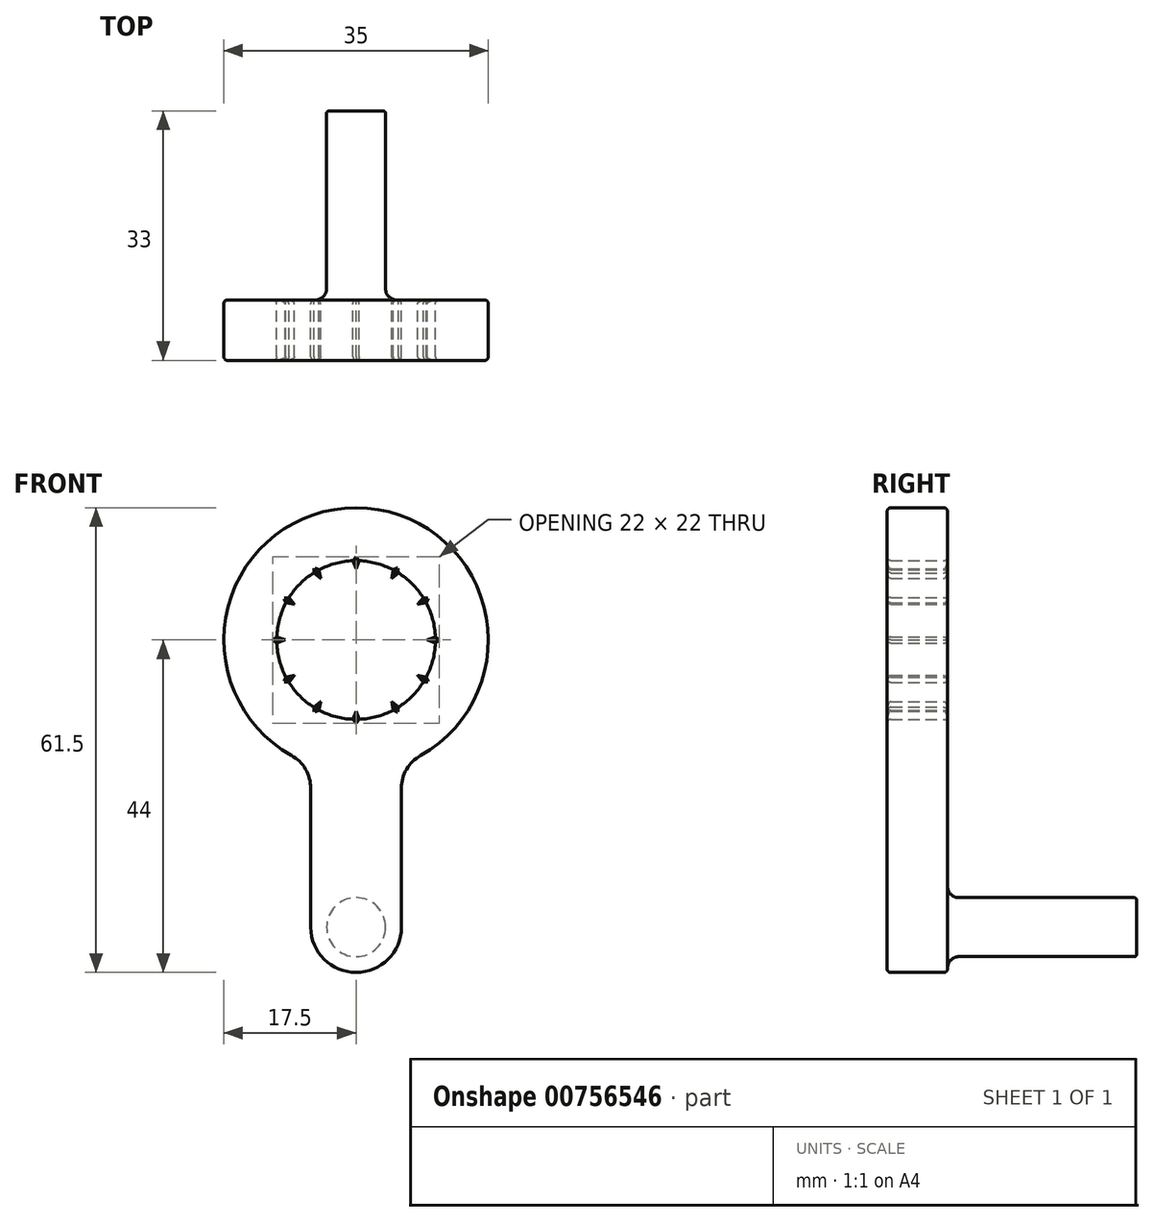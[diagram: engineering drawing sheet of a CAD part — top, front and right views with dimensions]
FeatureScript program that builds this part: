
annotation { "Feature Type Name" : "Feature", "Feature Type Description" : "" }
export const myFeature = defineFeature(function(context is Context, id is Id, definition is map)
    precondition{}
    {
        {
            var Q0;
            Q0=qCreatedBy(makeId("Front.planeOp"),FACE);
            var sketch = newSketch(context, id + "F0", { "sketchPlane" : qUnion([Q0])});
            skArc(sketch, "E0", {"start": v(8.56, -15.27) * mm, "mid": v(0, 17.5) * mm, "end": v(-8.56, -15.27) * mm});
            skCircle(sketch, "E1", {"center": v(0, 0) * mm, "radius": 9.4 * mm, "construction": true});
            skLineSegment(sketch, "E2", {"start": v(0, 109.46) * mm, "end": v(0, -98.11) * mm, "construction": true});
            skLineSegment(sketch, "E3", {"start": v(-338.44, 0) * mm, "end": v(369.24, 0) * mm, "construction": true});
            skLineSegment(sketch, "E4", {"start": v(-0.4, 10.5) * mm, "end": v(0, 9.4) * mm});
            skLineSegment(sketch, "E5.MirrorCS", {"start": v(0.4, 10.5) * mm, "end": v(0, 9.4) * mm});
            skLineSegment(sketch, "E6", {"start": v(0, 0) * mm, "end": v(63.84, 110.57) * mm, "construction": true});
            skArc(sketch, "E7", {"start": v(4.9, 9.29) * mm, "mid": v(2.72, 10.14) * mm, "end": v(0.4, 10.5) * mm});
            skLineSegment(sketch, "E8", {"start": v(0, 0) * mm, "end": v(0, -28.63) * mm, "construction": true});
            skLineSegment(sketch, "E9", {"start": v(-6, -19.63) * mm, "end": v(-6, -38) * mm});
            skLineSegment(sketch, "E10", {"start": v(0, -44) * mm, "end": v(0, -44) * mm});
            skLineSegment(sketch, "E11", {"start": v(6, -38) * mm, "end": v(6, -19.63) * mm});
            skPoint(sketch, "E12.visualSharp", {"position": v(-6, -44) * mm});
            skArc(sketch, "E12.filletArc", {"start": v(-6, -38) * mm, "mid": v(-4.24, -42.24) * mm, "end": v(0, -44) * mm});
            skPoint(sketch, "E13.visualSharp", {"position": v(6, -44) * mm});
            skArc(sketch, "E13.filletArc", {"start": v(0, -44) * mm, "mid": v(4.24, -42.24) * mm, "end": v(6, -38) * mm});
            skPoint(sketch, "E14.visualSharp", {"position": v(-6, -16.44) * mm});
            skArc(sketch, "E14.filletArc", {"start": v(-6, -19.63) * mm, "mid": v(-6.69, -17.1) * mm, "end": v(-8.56, -15.27) * mm});
            skPoint(sketch, "E15.visualSharp", {"position": v(6, -16.44) * mm});
            skArc(sketch, "E15.filletArc", {"start": v(8.56, -15.27) * mm, "mid": v(6.69, -17.1) * mm, "end": v(6, -19.63) * mm});
            skArc(sketch, "E16", {"start": v(1, -27.5) * mm, "mid": v(0, -26.5) * mm, "end": v(-1, -27.5) * mm, "construction": true});
            skArc(sketch, "E17", {"start": v(-1, -28) * mm, "mid": v(0, -29) * mm, "end": v(1, -28) * mm, "construction": true});
            skLineSegment(sketch, "E18", {"start": v(-1, -27.5) * mm, "end": v(-1, -28) * mm, "construction": true});
            skLineSegment(sketch, "E19", {"start": v(1, -27.5) * mm, "end": v(1, -28) * mm, "construction": true});
            skLineSegment(sketch, "E20.1.0", {"start": v(-4.9, 9.29) * mm, "end": v(-4.7, 8.14) * mm});
            skLineSegment(sketch, "E20.1.1", {"start": v(-5.6, 8.89) * mm, "end": v(-4.7, 8.14) * mm});
            skArc(sketch, "E20.1.2", {"start": v(-0.4, 10.5) * mm, "mid": v(-2.72, 10.14) * mm, "end": v(-4.9, 9.29) * mm});
            skLineSegment(sketch, "E20.2.0", {"start": v(-8.89, 5.6) * mm, "end": v(-8.14, 4.7) * mm});
            skLineSegment(sketch, "E20.2.1", {"start": v(-9.29, 4.9) * mm, "end": v(-8.14, 4.7) * mm});
            skArc(sketch, "E20.2.2", {"start": v(-5.6, 8.89) * mm, "mid": v(-7.42, 7.42) * mm, "end": v(-8.89, 5.6) * mm});
            skLineSegment(sketch, "E21.2.3.0", {"start": v(-10.5, 0.4) * mm, "end": v(-9.4, 0) * mm});
            skLineSegment(sketch, "E21.3.3.0", {"start": v(-10.5, -0.4) * mm, "end": v(-9.4, 0) * mm});
            skArc(sketch, "E21.6.3.0", {"start": v(-9.29, 4.9) * mm, "mid": v(-10.14, 2.72) * mm, "end": v(-10.5, 0.4) * mm});
            skLineSegment(sketch, "E21.2.4.0", {"start": v(-9.29, -4.9) * mm, "end": v(-8.14, -4.7) * mm});
            skLineSegment(sketch, "E21.3.4.0", {"start": v(-8.89, -5.6) * mm, "end": v(-8.14, -4.7) * mm});
            skArc(sketch, "E21.6.4.0", {"start": v(-10.5, -0.4) * mm, "mid": v(-10.14, -2.72) * mm, "end": v(-9.29, -4.9) * mm});
            skLineSegment(sketch, "E21.2.5.0", {"start": v(-5.6, -8.89) * mm, "end": v(-4.7, -8.14) * mm});
            skLineSegment(sketch, "E21.3.5.0", {"start": v(-4.9, -9.29) * mm, "end": v(-4.7, -8.14) * mm});
            skArc(sketch, "E21.6.5.0", {"start": v(-8.89, -5.6) * mm, "mid": v(-7.42, -7.42) * mm, "end": v(-5.6, -8.89) * mm});
            skLineSegment(sketch, "E21.2.6.0", {"start": v(-0.4, -10.5) * mm, "end": v(0, -9.4) * mm});
            skLineSegment(sketch, "E21.3.6.0", {"start": v(0.4, -10.5) * mm, "end": v(0, -9.4) * mm});
            skArc(sketch, "E21.6.6.0", {"start": v(-4.9, -9.29) * mm, "mid": v(-2.72, -10.14) * mm, "end": v(-0.4, -10.5) * mm});
            skLineSegment(sketch, "E21.2.7.0", {"start": v(4.9, -9.29) * mm, "end": v(4.7, -8.14) * mm});
            skLineSegment(sketch, "E21.3.7.0", {"start": v(5.6, -8.89) * mm, "end": v(4.7, -8.14) * mm});
            skArc(sketch, "E21.6.7.0", {"start": v(0.4, -10.5) * mm, "mid": v(2.72, -10.14) * mm, "end": v(4.9, -9.29) * mm});
            skLineSegment(sketch, "E21.2.8.0", {"start": v(8.89, -5.6) * mm, "end": v(8.14, -4.7) * mm});
            skLineSegment(sketch, "E21.3.8.0", {"start": v(9.29, -4.9) * mm, "end": v(8.14, -4.7) * mm});
            skArc(sketch, "E21.6.8.0", {"start": v(5.6, -8.89) * mm, "mid": v(7.42, -7.42) * mm, "end": v(8.89, -5.6) * mm});
            skLineSegment(sketch, "E21.2.9.0", {"start": v(10.5, -0.4) * mm, "end": v(9.4, 0) * mm});
            skLineSegment(sketch, "E21.3.9.0", {"start": v(10.5, 0.4) * mm, "end": v(9.4, 0) * mm});
            skArc(sketch, "E21.6.9.0", {"start": v(9.29, -4.9) * mm, "mid": v(10.14, -2.72) * mm, "end": v(10.5, -0.4) * mm});
            skLineSegment(sketch, "E21.2.10.0", {"start": v(9.29, 4.9) * mm, "end": v(8.14, 4.7) * mm});
            skLineSegment(sketch, "E21.3.10.0", {"start": v(8.89, 5.6) * mm, "end": v(8.14, 4.7) * mm});
            skArc(sketch, "E21.6.10.0", {"start": v(10.5, 0.4) * mm, "mid": v(10.14, 2.72) * mm, "end": v(9.29, 4.9) * mm});
            skLineSegment(sketch, "E21.2.11.0", {"start": v(5.6, 8.89) * mm, "end": v(4.7, 8.14) * mm});
            skLineSegment(sketch, "E21.3.11.0", {"start": v(4.9, 9.29) * mm, "end": v(4.7, 8.14) * mm});
            skArc(sketch, "E21.6.11.0", {"start": v(8.89, 5.6) * mm, "mid": v(7.42, 7.42) * mm, "end": v(5.6, 8.89) * mm});
            skSolve(sketch);
        }
        {
            var Q0;
            Q0=makeQuery(id+"F0.imprint","IMPRINT",FACE,{"disambiguationData":[TD([[makeQuery(id+"F0.imprint","IMPRINT",EDGE,{"derivedFrom":sQuery(id+"F0.wireOp",EDGE,"E0")}),1.0]])]});
            extrude(context, id + "F1", {"entities" : qUnion([Q0]), "depth" : 8 * mm, "offsetDistance" : 25 * mm});
        }
        {
            var Q0;
            Q0=makeQuery(id+"F1.opExtrude","CAP_FACE",FACE,{"disambiguationData":[OSD([sQuery(id+"F0.wireOp",EDGE,"E0"),sQuery(id+"F0.wireOp",EDGE,"E4"),sQuery(id+"F0.wireOp",EDGE,"E5.MirrorCS"),sQuery(id+"F0.wireOp",EDGE,"E7"),sQuery(id+"F0.wireOp",EDGE,"E9"),sQuery(id+"F0.wireOp",EDGE,"E10"),sQuery(id+"F0.wireOp",EDGE,"E11"),sQuery(id+"F0.wireOp",EDGE,"E12.filletArc"),sQuery(id+"F0.wireOp",EDGE,"E13.filletArc"),sQuery(id+"F0.wireOp",EDGE,"E14.filletArc"),sQuery(id+"F0.wireOp",EDGE,"E15.filletArc"),sQuery(id+"F0.wireOp",EDGE,"E20.1.0"),sQuery(id+"F0.wireOp",EDGE,"E20.1.1"),sQuery(id+"F0.wireOp",EDGE,"E20.1.2"),sQuery(id+"F0.wireOp",EDGE,"E20.2.0"),sQuery(id+"F0.wireOp",EDGE,"E20.2.1"),sQuery(id+"F0.wireOp",EDGE,"E20.2.2"),sQuery(id+"F0.wireOp",EDGE,"E21.2.3.0"),sQuery(id+"F0.wireOp",EDGE,"E21.3.3.0"),sQuery(id+"F0.wireOp",EDGE,"E21.6.3.0"),sQuery(id+"F0.wireOp",EDGE,"E21.2.4.0"),sQuery(id+"F0.wireOp",EDGE,"E21.3.4.0"),sQuery(id+"F0.wireOp",EDGE,"E21.6.4.0"),sQuery(id+"F0.wireOp",EDGE,"E21.2.5.0"),sQuery(id+"F0.wireOp",EDGE,"E21.3.5.0"),sQuery(id+"F0.wireOp",EDGE,"E21.6.5.0"),sQuery(id+"F0.wireOp",EDGE,"E21.2.6.0"),sQuery(id+"F0.wireOp",EDGE,"E21.3.6.0"),sQuery(id+"F0.wireOp",EDGE,"E21.6.6.0"),sQuery(id+"F0.wireOp",EDGE,"E21.2.7.0"),sQuery(id+"F0.wireOp",EDGE,"E21.3.7.0"),sQuery(id+"F0.wireOp",EDGE,"E21.6.7.0"),sQuery(id+"F0.wireOp",EDGE,"E21.2.8.0"),sQuery(id+"F0.wireOp",EDGE,"E21.3.8.0"),sQuery(id+"F0.wireOp",EDGE,"E21.6.8.0"),sQuery(id+"F0.wireOp",EDGE,"E21.2.9.0"),sQuery(id+"F0.wireOp",EDGE,"E21.3.9.0"),sQuery(id+"F0.wireOp",EDGE,"E21.6.9.0"),sQuery(id+"F0.wireOp",EDGE,"E21.2.10.0"),sQuery(id+"F0.wireOp",EDGE,"E21.3.10.0"),sQuery(id+"F0.wireOp",EDGE,"E21.6.10.0"),sQuery(id+"F0.wireOp",EDGE,"E21.2.11.0"),sQuery(id+"F0.wireOp",EDGE,"E21.3.11.0"),sQuery(id+"F0.wireOp",EDGE,"E21.6.11.0")])],"isStart":true});
            var sketch = newSketch(context, id + "F2", { "sketchPlane" : qUnion([Q0])});
            skSolve(sketch);
        }
        {
            var Q0;
            Q0=makeQuery(id+"F1.opExtrude","CAP_FACE",FACE,{"disambiguationData":[OSD([sQuery(id+"F0.wireOp",EDGE,"E0"),sQuery(id+"F0.wireOp",EDGE,"E4"),sQuery(id+"F0.wireOp",EDGE,"E5.MirrorCS"),sQuery(id+"F0.wireOp",EDGE,"E7"),sQuery(id+"F0.wireOp",EDGE,"E9"),sQuery(id+"F0.wireOp",EDGE,"E10"),sQuery(id+"F0.wireOp",EDGE,"E11"),sQuery(id+"F0.wireOp",EDGE,"E12.filletArc"),sQuery(id+"F0.wireOp",EDGE,"E13.filletArc"),sQuery(id+"F0.wireOp",EDGE,"E14.filletArc"),sQuery(id+"F0.wireOp",EDGE,"E15.filletArc"),sQuery(id+"F0.wireOp",EDGE,"E20.1.0"),sQuery(id+"F0.wireOp",EDGE,"E20.1.1"),sQuery(id+"F0.wireOp",EDGE,"E20.1.2"),sQuery(id+"F0.wireOp",EDGE,"E20.2.0"),sQuery(id+"F0.wireOp",EDGE,"E20.2.1"),sQuery(id+"F0.wireOp",EDGE,"E20.2.2"),sQuery(id+"F0.wireOp",EDGE,"E21.2.3.0"),sQuery(id+"F0.wireOp",EDGE,"E21.3.3.0"),sQuery(id+"F0.wireOp",EDGE,"E21.6.3.0"),sQuery(id+"F0.wireOp",EDGE,"E21.2.4.0"),sQuery(id+"F0.wireOp",EDGE,"E21.3.4.0"),sQuery(id+"F0.wireOp",EDGE,"E21.6.4.0"),sQuery(id+"F0.wireOp",EDGE,"E21.2.5.0"),sQuery(id+"F0.wireOp",EDGE,"E21.3.5.0"),sQuery(id+"F0.wireOp",EDGE,"E21.6.5.0"),sQuery(id+"F0.wireOp",EDGE,"E21.2.6.0"),sQuery(id+"F0.wireOp",EDGE,"E21.3.6.0"),sQuery(id+"F0.wireOp",EDGE,"E21.6.6.0"),sQuery(id+"F0.wireOp",EDGE,"E21.2.7.0"),sQuery(id+"F0.wireOp",EDGE,"E21.3.7.0"),sQuery(id+"F0.wireOp",EDGE,"E21.6.7.0"),sQuery(id+"F0.wireOp",EDGE,"E21.2.8.0"),sQuery(id+"F0.wireOp",EDGE,"E21.3.8.0"),sQuery(id+"F0.wireOp",EDGE,"E21.6.8.0"),sQuery(id+"F0.wireOp",EDGE,"E21.2.9.0"),sQuery(id+"F0.wireOp",EDGE,"E21.3.9.0"),sQuery(id+"F0.wireOp",EDGE,"E21.6.9.0"),sQuery(id+"F0.wireOp",EDGE,"E21.2.10.0"),sQuery(id+"F0.wireOp",EDGE,"E21.3.10.0"),sQuery(id+"F0.wireOp",EDGE,"E21.6.10.0"),sQuery(id+"F0.wireOp",EDGE,"E21.2.11.0"),sQuery(id+"F0.wireOp",EDGE,"E21.3.11.0"),sQuery(id+"F0.wireOp",EDGE,"E21.6.11.0")])],"isStart":false});
            fillet(context, id + "F3", {"entities" : qUnion([Q0]), "radius" : 0.5 * mm, "tangentPropagation" : true, "allowEdgeOverflow" : false});
        }
        {
            var Q0;
            Q0=makeQuery(id+"F1.opExtrude","CAP_FACE",FACE,{"disambiguationData":[OSD([sQuery(id+"F0.wireOp",EDGE,"E0"),sQuery(id+"F0.wireOp",EDGE,"E4"),sQuery(id+"F0.wireOp",EDGE,"E5.MirrorCS"),sQuery(id+"F0.wireOp",EDGE,"E7"),sQuery(id+"F0.wireOp",EDGE,"E9"),sQuery(id+"F0.wireOp",EDGE,"E10"),sQuery(id+"F0.wireOp",EDGE,"E11"),sQuery(id+"F0.wireOp",EDGE,"E12.filletArc"),sQuery(id+"F0.wireOp",EDGE,"E13.filletArc"),sQuery(id+"F0.wireOp",EDGE,"E14.filletArc"),sQuery(id+"F0.wireOp",EDGE,"E15.filletArc"),sQuery(id+"F0.wireOp",EDGE,"E20.1.0"),sQuery(id+"F0.wireOp",EDGE,"E20.1.1"),sQuery(id+"F0.wireOp",EDGE,"E20.1.2"),sQuery(id+"F0.wireOp",EDGE,"E20.2.0"),sQuery(id+"F0.wireOp",EDGE,"E20.2.1"),sQuery(id+"F0.wireOp",EDGE,"E20.2.2"),sQuery(id+"F0.wireOp",EDGE,"E21.2.3.0"),sQuery(id+"F0.wireOp",EDGE,"E21.3.3.0"),sQuery(id+"F0.wireOp",EDGE,"E21.6.3.0"),sQuery(id+"F0.wireOp",EDGE,"E21.2.4.0"),sQuery(id+"F0.wireOp",EDGE,"E21.3.4.0"),sQuery(id+"F0.wireOp",EDGE,"E21.6.4.0"),sQuery(id+"F0.wireOp",EDGE,"E21.2.5.0"),sQuery(id+"F0.wireOp",EDGE,"E21.3.5.0"),sQuery(id+"F0.wireOp",EDGE,"E21.6.5.0"),sQuery(id+"F0.wireOp",EDGE,"E21.2.6.0"),sQuery(id+"F0.wireOp",EDGE,"E21.3.6.0"),sQuery(id+"F0.wireOp",EDGE,"E21.6.6.0"),sQuery(id+"F0.wireOp",EDGE,"E21.2.7.0"),sQuery(id+"F0.wireOp",EDGE,"E21.3.7.0"),sQuery(id+"F0.wireOp",EDGE,"E21.6.7.0"),sQuery(id+"F0.wireOp",EDGE,"E21.2.8.0"),sQuery(id+"F0.wireOp",EDGE,"E21.3.8.0"),sQuery(id+"F0.wireOp",EDGE,"E21.6.8.0"),sQuery(id+"F0.wireOp",EDGE,"E21.2.9.0"),sQuery(id+"F0.wireOp",EDGE,"E21.3.9.0"),sQuery(id+"F0.wireOp",EDGE,"E21.6.9.0"),sQuery(id+"F0.wireOp",EDGE,"E21.2.10.0"),sQuery(id+"F0.wireOp",EDGE,"E21.3.10.0"),sQuery(id+"F0.wireOp",EDGE,"E21.6.10.0"),sQuery(id+"F0.wireOp",EDGE,"E21.2.11.0"),sQuery(id+"F0.wireOp",EDGE,"E21.3.11.0"),sQuery(id+"F0.wireOp",EDGE,"E21.6.11.0")])],"isStart":true});
            var Q1;
            Q1=makeQuery(id+"FsdE2l80Q1M4T3P_1.opExtrude","SWEPT_FACE",FACE,{"disambiguationData":[OSD([sQuery(id+"F2.wireOp",EDGE,"bn6XExdd-CKR3-WdK1-uQBg-iD7gCpoWDGnA")])]});
            fillet(context, id + "F4", {"entities" : qUnion([Q0, Q1]), "radius" : 0.5 * mm, "tangentPropagation" : true, "allowEdgeOverflow" : false});
        }
        {
            var Q0;
            Q0=qCreatedBy(makeId("Right.planeOp"),FACE);
            var sketch = newSketch(context, id + "F5", { "sketchPlane" : qUnion([Q0])});
            skLineSegment(sketch, "E22", {"start": v(0, -38) * mm, "end": v(27.5, -38) * mm, "construction": true});
            skLineSegment(sketch, "E23", {"start": v(0, -38) * mm, "end": v(25, -38) * mm});
            skLineSegment(sketch, "E24", {"start": v(25, -38) * mm, "end": v(25, -34.4) * mm});
            skLineSegment(sketch, "E25", {"start": v(24.7, -34.1) * mm, "end": v(1.5, -34.1) * mm});
            skArc(sketch, "E26", {"start": v(0, -32.6) * mm, "mid": v(0.44, -33.66) * mm, "end": v(1.5, -34.1) * mm});
            skLineSegment(sketch, "E27", {"start": v(0, -32.6) * mm, "end": v(0, -38) * mm});
            skPoint(sketch, "E28.visualSharp", {"position": v(25, -34.1) * mm});
            skArc(sketch, "E28.filletArc", {"start": v(25, -34.4) * mm, "mid": v(24.91, -34.19) * mm, "end": v(24.7, -34.1) * mm});
            skSolve(sketch);
        }
        {
            var Q0;
            Q0=makeQuery(id+"F5.imprint","IMPRINT",FACE,{"disambiguationData":[TD([[makeQuery(id+"F5.imprint","IMPRINT",EDGE,{"derivedFrom":sQuery(id+"F5.wireOp",EDGE,"E23")}),1.0]])]});
            var Q1;
            Q1=sQuery(id+"F5.wireOp",EDGE,"E22");
            revolve(context, id + "F6", {"operationType" : NewBodyOperationType.ADD, "surfaceOperationType" : NewSurfaceOperationType.NEW, "entities" : qUnion([Q0]), "axis" : qUnion([Q1]), "revolveType" : RevolveType.FULL});
        }
    });
